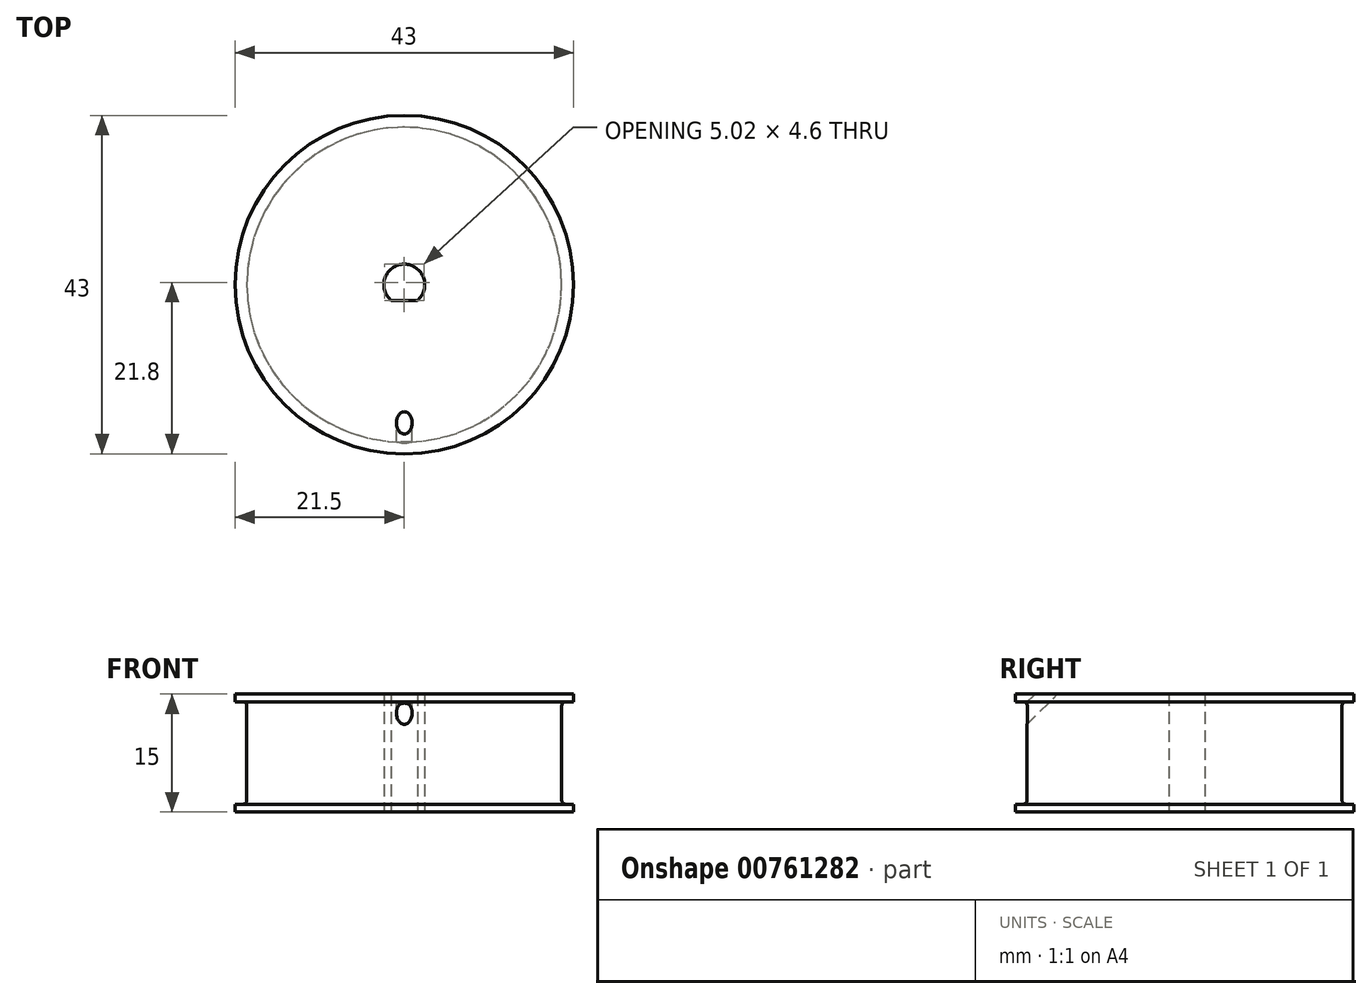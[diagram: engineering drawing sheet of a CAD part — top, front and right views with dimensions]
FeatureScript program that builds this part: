
annotation { "Feature Type Name" : "Feature", "Feature Type Description" : "" }
export const myFeature = defineFeature(function(context is Context, id is Id, definition is map)
    precondition{}
    {
        {
            var Q0;
            Q0=qCreatedBy(makeId("Front.planeOp"),FACE);
            var sketch = newSketch(context, id + "F0", { "sketchPlane" : qUnion([Q0])});
            skLineSegment(sketch, "E0", {"start": v(2.6, 0) * mm, "end": v(21.5, 0) * mm});
            skLineSegment(sketch, "E1", {"start": v(21.5, 15) * mm, "end": v(2.6, 15) * mm});
            skLineSegment(sketch, "E2", {"start": v(2.6, 15) * mm, "end": v(2.6, 0) * mm});
            skLineSegment(sketch, "E3", {"start": v(0, 0) * mm, "end": v(0, 6.75) * mm, "construction": true});
            skLineSegment(sketch, "E4", {"start": v(21.5, 15) * mm, "end": v(21.5, 14) * mm});
            skLineSegment(sketch, "E5", {"start": v(21.5, 14) * mm, "end": v(20.5, 14) * mm});
            skLineSegment(sketch, "E6", {"start": v(20, 13.5) * mm, "end": v(20, 1.5) * mm});
            skLineSegment(sketch, "E7", {"start": v(20.5, 1) * mm, "end": v(21.5, 1) * mm});
            skLineSegment(sketch, "E8", {"start": v(21.5, 1) * mm, "end": v(21.5, 0) * mm});
            skPoint(sketch, "E9.visualSharp", {"position": v(20, 14) * mm});
            skArc(sketch, "E9.filletArc", {"start": v(20.5, 14) * mm, "mid": v(20.15, 13.85) * mm, "end": v(20, 13.5) * mm});
            skPoint(sketch, "E10.visualSharp", {"position": v(20, 1) * mm});
            skArc(sketch, "E10.filletArc", {"start": v(20, 1.5) * mm, "mid": v(20.15, 1.15) * mm, "end": v(20.5, 1) * mm});
            skSolve(sketch);
        }
        {
            var Q0;
            Q0 = qSketchRegion(id + "F0", true);
            var Q1;
            Q1=sQuery(id+"F0.wireOp",EDGE,"E3");
            revolve(context, id + "F1", {"surfaceOperationType" : NewSurfaceOperationType.NEW, "entities" : qUnion([Q0]), "axis" : qUnion([Q1]), "revolveType" : RevolveType.FULL});
        }
        {
            var Q0;
            Q0=qCreatedBy(makeId("Top.planeOp"),FACE);
            var sketch = newSketch(context, id + "F2", { "sketchPlane" : qUnion([Q0])});
            skLineSegment(sketch, "E11", {"start": v(-1.66, -2) * mm, "end": v(1.66, -2) * mm});
            skArc(sketch, "E12.0", {"start": v(-1.66, -2) * mm, "mid": v(0, -2.6) * mm, "end": v(1.66, -2) * mm});
            skSolve(sketch);
        }
        {
            var Q0;
            Q0 = qSketchRegion(id + "F2", true);
            var Q1;
            Q1=makeQuery(id+"F1.opRevolve","SWEPT_FACE",FACE,{"disambiguationData":[OSD([sQuery(id+"F0.wireOp",EDGE,"E1")])]});
            extrude(context, id + "F3", {"entities" : qUnion([Q0]), "operationType" : NewBodyOperationType.ADD, "endBound" : BoundingType.UP_TO_SURFACE, "depth" : 25 * mm, "endBoundEntityFace" : qUnion([Q1]), "offsetDistance" : 25 * mm});
        }
        {
            var Q0;
            Q0=makeQuery(id+"F3.opExtrude","CAP_EDGE",EDGE,{"disambiguationData":[OSD([sQuery(id+"F2.wireOp",EDGE,"E11")])],"isStart":false});
            cPlane(context, id + "F4", {"entities" : qUnion([Q0]), "cplaneType" : CPlaneType.LINE_ANGLE, "offset" : 25 * mm, "angle" : 45 * degree, "width" : 150 * mm, "height" : 150 * mm});
        }
        {
            var Q0;
            Q0=qCreatedBy(id+"F4.planeOp",FACE);
            var sketch = newSketch(context, id + "F5", { "sketchPlane" : qUnion([Q0])});
            skCircle(sketch, "E13", {"center": v(0, 23.02) * mm, "radius": 1 * mm});
            skSolve(sketch);
        }
        {
            var Q0;
            Q0 = qSketchRegion(id + "F5", true);
            extrude(context, id + "F6", {"entities" : qUnion([Q0]), "operationType" : NewBodyOperationType.REMOVE, "oppositeDirection" : true, "depth" : 25 * mm, "offsetDistance" : 25 * mm});
        }
    });
